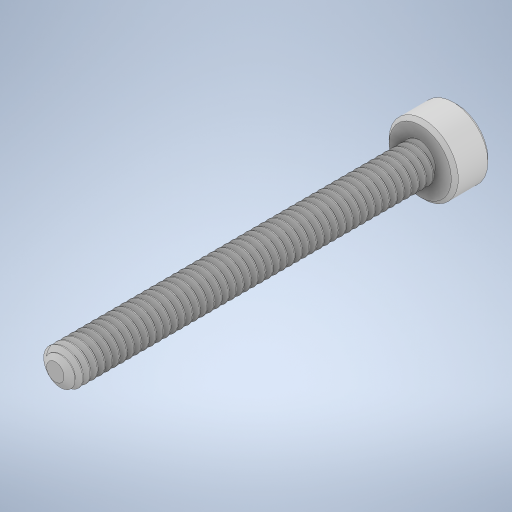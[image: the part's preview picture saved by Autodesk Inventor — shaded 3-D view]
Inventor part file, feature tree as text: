
AUTODESK INVENTOR PART (.ipt)
format: ipt  version: 2024 (Build 280153000, 153)  size: 1,434,624 bytes
history: native  units: mm
features: other x1, chamfer x1
ambient origin geometry x8: Origin, YZ Plane, XZ Plane, XY Plane, X Axis, Y Axis, Z Axis, Center Point
bodies: Body1 (feature_tree)
feature tree (2):
  other  "Těleso1"
  chamfer  "Chamfer1"  [1 undecoded]
note: 1 required parameter value undecoded (feature->parameter linkage not recoverable at this tier; creation-order binding heuristic only, values carry confidence <= 0.55)
